FCSTD DOCUMENT  (FreeCAD 0.19R)
Label: CAD wingTip
License: All rights reserved
LicenseURL: http://en.wikipedia.org/wiki/All_rights_reserved
objects: Sketcher::SketchObject×1
note: 1 computed .brp shape members not serialized (recipe doc carries the construction recipe); baked Part::Feature solids carry a one-line shape summary decoded from their .brp

FEATURE [Sketcher::SketchObject] Sketch
  FullyConstrained = true
  sketch-geometry (15):
    g0: LineSegment StartX=0 StartY=0 StartZ=0 EndX=3228.3 EndY=0 EndZ=0
    g1: LineSegment StartX=244.606 StartY=291.51 StartZ=0 EndX=3024.21 EndY=291.51 EndZ=0
    g2: LineSegment StartX=866.807 StartY=1033.02 StartZ=0 EndX=2504.81 EndY=1033.02 EndZ=0
    g3: LineSegment StartX=1954.28 StartY=2329.02 StartZ=0 EndX=3412.28 EndY=2329.02 EndZ=0
    g4: LineSegment StartX=2504.81 StartY=1033.02 StartZ=0 EndX=3228.3 EndY=0 EndZ=0
    g5: LineSegment StartX=3170.97 StartY=3779.02 StartZ=0 EndX=3180.97 EndY=3779.02 EndZ=0
    g6: LineSegment StartX=3180.97 StartY=3779.02 StartZ=0 EndX=3966.22 EndY=3120.12 EndZ=0
    g7: LineSegment StartX=3966.22 StartY=3120.12 StartZ=0 EndX=2618.09 EndY=3120.12 EndZ=0
    g8: LineSegment StartX=3966.22 StartY=3120.12 StartZ=0 EndX=3412.28 EndY=2329.02 EndZ=0
    g9: LineSegment StartX=3412.28 StartY=2329.02 StartZ=0 EndX=2504.81 EndY=1033.02 EndZ=0
    g10: LineSegment StartX=3170.97 StartY=3779.02 StartZ=0 EndX=2618.09 EndY=3120.12 EndZ=0
    g11: LineSegment StartX=244.606 StartY=291.51 StartZ=0 EndX=866.807 EndY=1033.02 EndZ=0
    g12: LineSegment StartX=866.807 StartY=1033.02 StartZ=0 EndX=1954.28 EndY=2329.02 EndZ=0
    g13: LineSegment StartX=1954.28 StartY=2329.02 StartZ=0 EndX=2618.09 EndY=3120.12 EndZ=0
    g14: LineSegment StartX=244.606 StartY=291.51 StartZ=0 EndX=-2.84e-14 EndY=0 EndZ=0
  constraints (46):
    c: Coincident(g0,g-1)
    c: PointOnObject(g0,g-1)
    c: Distance(g0) = 3228.3
    c: Horizontal(g1)
    c: Distance(g1) = 2779.6
    c: DistanceY(g0,g1) = 291.51
    c: Horizontal(g2)
    c: Distance(g2) = 1638
    c: DistanceY(g1,g2) = 741.51
    c: Horizontal(g3)
    c: Distance(g3) = 1458
    c: DistanceY(g2,g3) = 1296
    c: DistanceY(g3,g5) = 1450
    c: DistanceY(g0,g5) = 3779.02
    c: Coincident(g4,g2)
    c: Coincident(g4,g0)
    c: Angle(g4,g0) = 0.959824
    c: Horizontal(g5)
    c: Coincident(g6,g5)
    c: Distance(g5) = 10
    c: Coincident(g7,g6)
    c: Horizontal(g7)
    c: Coincident(g8,g6)
    c: Coincident(g8,g3)
    c: Coincident(g9,g3)
    c: Coincident(g9,g2)
    c: Parallel(g8,g9)
    c: Distance(g7) = 1348.12
    c: Coincident(g10,g5)
    c: Coincident(g10,g7)
    c: Coincident(g11,g1)
    c: Coincident(g11,g2)
    c: Coincident(g12,g2)
    c: Coincident(g12,g3)
    c: Coincident(g13,g3)
    c: Coincident(g13,g7)
    c: Parallel(g11,g12)
    c: Parallel(g12,g13)
    c: Parallel(g13,g10)
    c: Angle(g10,g6) = 1.5708
    c: Coincident(g14,g1)
    c: Coincident(g14,g0)
    c: Parallel(g11,g14)
    c: Angle(g0,g14) = 0.872665
    c: DistanceY(g3,g6) = 791.102
    c: DistanceY(g6,g5) = 658.898
